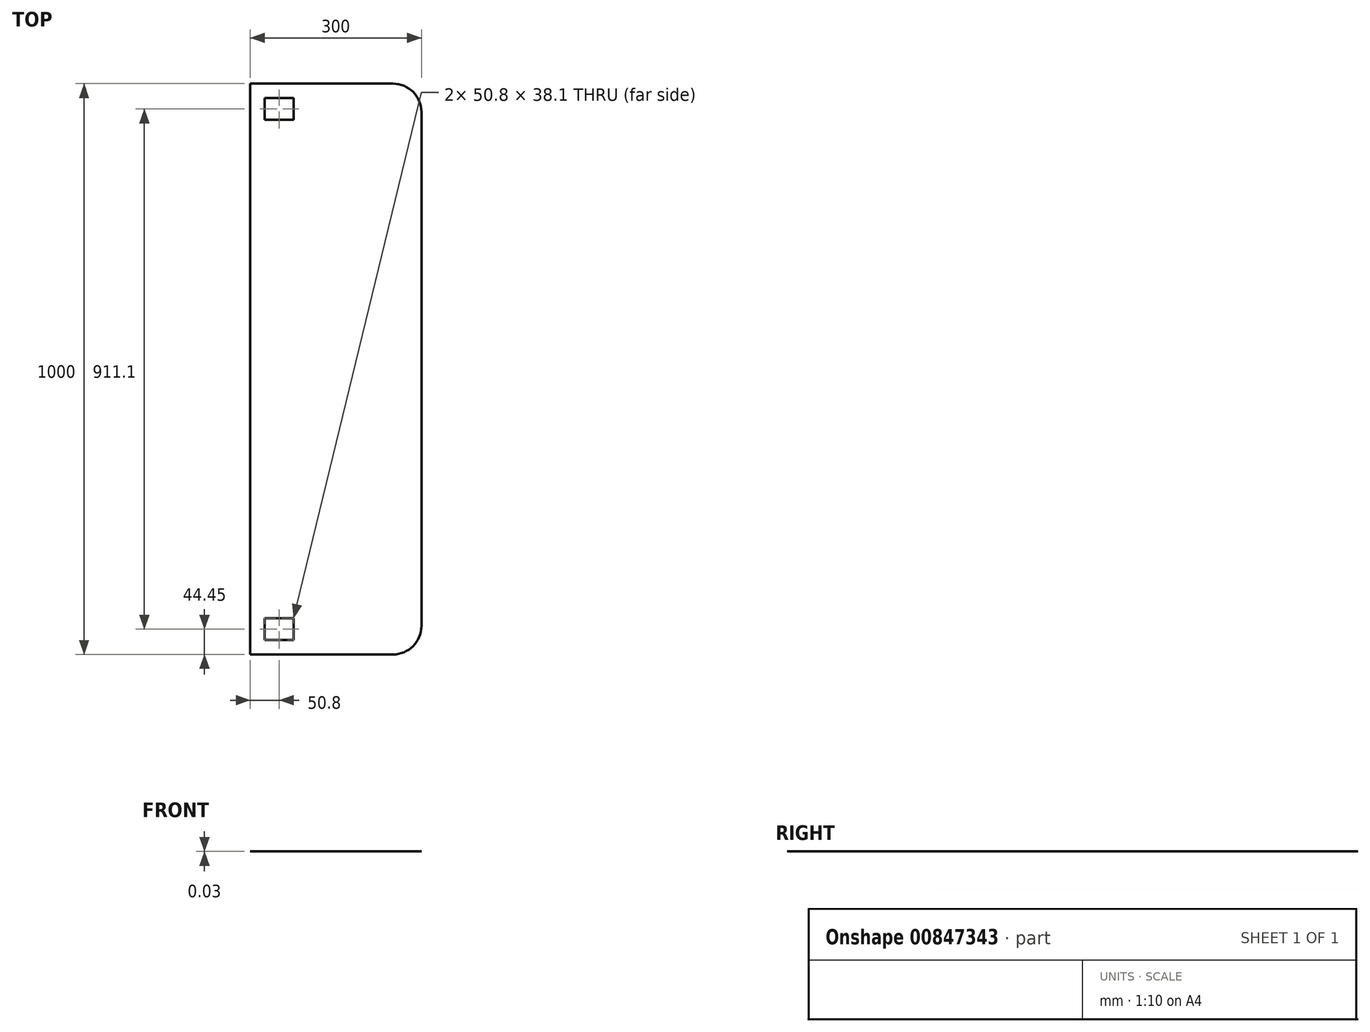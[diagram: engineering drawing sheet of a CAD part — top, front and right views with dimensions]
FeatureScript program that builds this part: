
annotation { "Feature Type Name" : "Feature", "Feature Type Description" : "" }
export const myFeature = defineFeature(function(context is Context, id is Id, definition is map)
    precondition{}
    {
        {
            var Q0;
            Q0=qCreatedBy(makeId("Top.planeOp"),FACE);
            var sketch = newSketch(context, id + "F0", { "sketchPlane" : qUnion([Q0])});
            skLineSegment(sketch, "E0.bottom", {"start": v(0, 0) * mm, "end": v(300, 0) * mm});
            skLineSegment(sketch, "E0.top", {"start": v(0, 1000) * mm, "end": v(300, 1000) * mm});
            skLineSegment(sketch, "E0.left", {"start": v(0, 0) * mm, "end": v(0, 1000) * mm});
            skLineSegment(sketch, "E0.right", {"start": v(300, 0) * mm, "end": v(300, 1000) * mm});
            skSolve(sketch);
        }
        {
            var Q0;
            Q0=makeQuery(id+"F0.imprint","IMPRINT",FACE,{"disambiguationData":[TD([[makeQuery(id+"F0.imprint","IMPRINT",EDGE,{"derivedFrom":sQuery(id+"F0.wireOp",EDGE,"E0.bottom")}),1.0]])]});
            extrude(context, id + "F1", {"entities" : qUnion([Q0]), "depth" : 3 / 101.6 * mm, "offsetDistance" : 25 * mm});
        }
        {
            var Q0;
            Q0=makeQuery(id+"F1.opExtrude","CAP_FACE",FACE,{"disambiguationData":[OSD([sQuery(id+"F0.wireOp",EDGE,"E0.bottom"),sQuery(id+"F0.wireOp",EDGE,"E0.top"),sQuery(id+"F0.wireOp",EDGE,"E0.left"),sQuery(id+"F0.wireOp",EDGE,"E0.right")])],"isStart":false});
            var sketch = newSketch(context, id + "F2", { "sketchPlane" : qUnion([Q0])});
            skLineSegment(sketch, "E1.bottom", {"start": v(25.4, 25.4) * mm, "end": v(76.2, 25.4) * mm});
            skLineSegment(sketch, "E1.top", {"start": v(25.4, 63.5) * mm, "end": v(76.2, 63.5) * mm});
            skLineSegment(sketch, "E1.left", {"start": v(25.4, 25.4) * mm, "end": v(25.4, 63.5) * mm});
            skLineSegment(sketch, "E1.right", {"start": v(76.2, 25.4) * mm, "end": v(76.2, 63.5) * mm});
            skLineSegment(sketch, "E2.bottom", {"start": v(76.2, 936.5) * mm, "end": v(25.4, 936.5) * mm});
            skLineSegment(sketch, "E2.top", {"start": v(76.2, 974.6) * mm, "end": v(25.4, 974.6) * mm});
            skLineSegment(sketch, "E2.left", {"start": v(76.2, 936.5) * mm, "end": v(76.2, 974.6) * mm});
            skLineSegment(sketch, "E2.right", {"start": v(25.4, 936.5) * mm, "end": v(25.4, 974.6) * mm});
            skSolve(sketch);
        }
        {
            var Q0;
            Q0=makeQuery(id+"F2.imprint","IMPRINT",FACE,{"disambiguationData":[TD([[makeQuery(id+"F2.imprint","IMPRINT",EDGE,{"derivedFrom":sQuery(id+"F2.wireOp",EDGE,"E1.bottom")}),1.0]])]});
            var Q1;
            Q1=makeQuery(id+"F2.imprint","IMPRINT",FACE,{"disambiguationData":[TD([[makeQuery(id+"F2.imprint","IMPRINT",EDGE,{"derivedFrom":sQuery(id+"F2.wireOp",EDGE,"E2.bottom")}),-1.0]])]});
            extrude(context, id + "F3", {"entities" : qUnion([Q0, Q1]), "operationType" : NewBodyOperationType.REMOVE, "endBound" : BoundingType.UP_TO_NEXT, "oppositeDirection" : true, "depth" : 25 * mm, "offsetDistance" : 25 * mm});
        }
        {
            var Q0;
            Q0=makeQuery(id+"F1.opExtrude","SWEPT_EDGE",EDGE,{"disambiguationData":[OSD([sQuery(id+"F0.wireOp",EDGE,"E0.bottom"),sQuery(id+"F0.wireOp",EDGE,"E0.right")])]});
            var Q1;
            Q1=makeQuery(id+"F1.opExtrude","SWEPT_EDGE",EDGE,{"disambiguationData":[OSD([sQuery(id+"F0.wireOp",EDGE,"E0.top"),sQuery(id+"F0.wireOp",EDGE,"E0.right")])]});
            fillet(context, id + "F4", {"entities" : qUnion([Q0, Q1]), "radius" : 50 * mm, "tangentPropagation" : true, "allowEdgeOverflow" : false});
        }
    });
